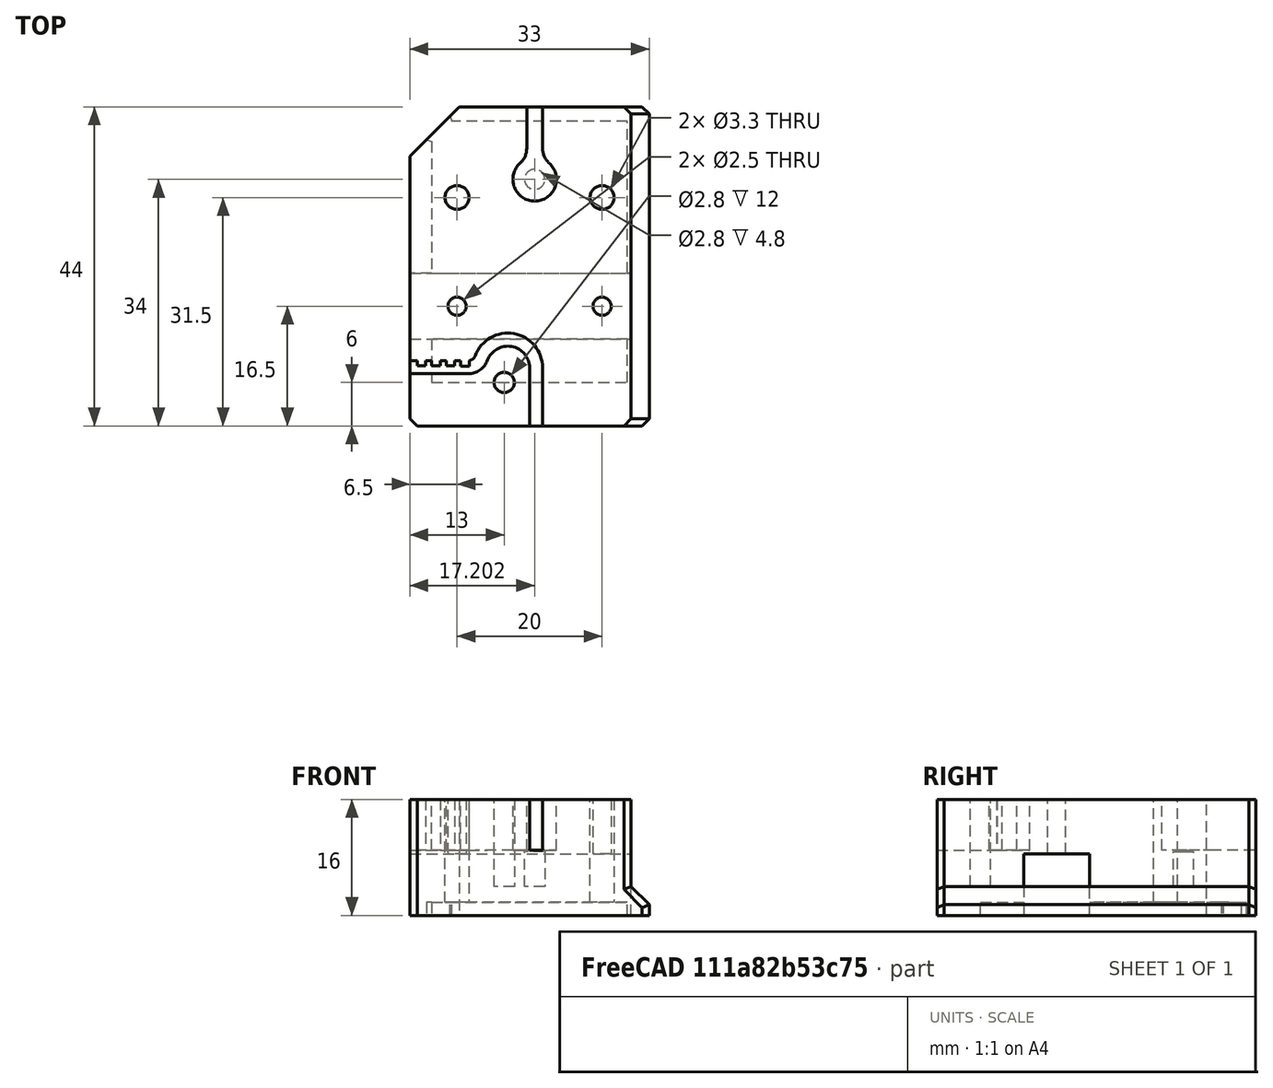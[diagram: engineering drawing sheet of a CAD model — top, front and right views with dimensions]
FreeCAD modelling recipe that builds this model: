
FCSTD DOCUMENT  (FreeCAD 0.19R)
Label: XjointBolted
License: All rights reserved
LicenseURL: http://en.wikipedia.org/wiki/All_rights_reserved
objects: Sketcher::SketchObject×10, PartDesign::Pocket×7, PartDesign::Pad×3, PartDesign::Chamfer×2, PartDesign::Body×1, Mesh::Feature×1
note: 35 computed .brp shape members not serialized (recipe doc carries the construction recipe); baked Part::Feature solids carry a one-line shape summary decoded from their .brp

FEATURE [Sketcher::SketchObject] Sketch005
  FullyConstrained = false
  MapMode = 5
  Support = -> [XY_Plane003]
  sketch-geometry (11):
    g0: LineSegment StartX=-37.8782 StartY=-3 StartZ=0 EndX=35.272 EndY=-3 EndZ=0
    g1: LineSegment StartX=35.272 StartY=-3 StartZ=0 EndX=35.272 EndY=-12 EndZ=0
    g2: LineSegment StartX=35.272 StartY=-12 StartZ=0 EndX=-37.8782 EndY=-12 EndZ=0
    g3: LineSegment StartX=-37.8782 StartY=-12 StartZ=0 EndX=-37.8782 EndY=-3 EndZ=0
    g4: LineSegment StartX=-44.3491 StartY=-7.5 StartZ=0 EndX=45.9652 EndY=-7.5 EndZ=0
    g5: Circle CenterX=-11.1499 CenterY=11.8637 CenterZ=0 NormalX=0 NormalY=0 NormalZ=1 AngleXU=0 Radius=1.40675
    g6: Circle CenterX=9.8811 CenterY=13.2001 CenterZ=0 NormalX=0 NormalY=0 NormalZ=1 AngleXU=0 Radius=2.36339
    g7: LineSegment StartX=-16.5 StartY=20 StartZ=0 EndX=16.5 EndY=20 EndZ=0
    g8: LineSegment StartX=16.5 StartY=20 StartZ=0 EndX=16.5 EndY=-24 EndZ=0
    g9: LineSegment StartX=16.5 StartY=-24 StartZ=0 EndX=-16.5 EndY=-24 EndZ=0
    g10: LineSegment StartX=-16.5 StartY=-24 StartZ=0 EndX=-16.5 EndY=20 EndZ=0
  constraints (22):
    c: Coincident(g0,g1)
    c: Coincident(g1,g2)
    c: Coincident(g2,g3)
    c: Coincident(g3,g0)
    c: Horizontal(g0)
    c: Horizontal(g2)
    c: Vertical(g1)
    c: Vertical(g3)
    c: Symmetric(g1,g0,g4)
    c: Distance(g1) = 9
    c: DistanceY(g4) = -7.5
    c: Coincident(g7,g8)
    c: Coincident(g8,g9)
    c: Coincident(g9,g10)
    c: Coincident(g10,g7)
    c: Horizontal(g7)
    c: Vertical(g8)
    c: Vertical(g10)
    c: Distance(g7) = 33
    c: DistanceY(g7) = 20
    c: DistanceY(g8) = -24
    c: Symmetric(g8,g9,g-2)
FEATURE [PartDesign::Pad] Pad002
  Direction = (1,1,1)
  Length = 16
  Length2 = 100
  Profile = -> Sketch005
  Type = 0
FEATURE [Sketcher::SketchObject] Sketch006  label="BottomPocket"
  FullyConstrained = true
  MapMode = 5
  Placement = pos=(0,0,0) rot=(1,0,0;3.14159rad)
  Support = -> [Pad002]
  sketch-geometry (4):
    g0: LineSegment StartX=-13.5 StartY=18 StartZ=0 EndX=13.5 EndY=18 EndZ=0
    g1: LineSegment StartX=13.5 StartY=18 StartZ=0 EndX=13.5 EndY=-18 EndZ=0
    g2: LineSegment StartX=13.5 StartY=-18 StartZ=0 EndX=-13.5 EndY=-18 EndZ=0
    g3: LineSegment StartX=-13.5 StartY=-18 StartZ=0 EndX=-13.5 EndY=18 EndZ=0
  constraints (11):
    c: Coincident(g0,g1)
    c: Coincident(g1,g2)
    c: Coincident(g2,g3)
    c: Coincident(g3,g0)
    c: Horizontal(g0)
    c: Horizontal(g2)
    c: Vertical(g1)
    c: Vertical(g3)
    c: Distance(g0) = 27
    c: Distance(g1) = 36
    c: Symmetric(g0,g2,g-1)
FEATURE [PartDesign::Pocket] Pocket002
  BaseFeature = -> Pad002
  Length = 1.8
  Length2 = 100
  Profile = -> Sketch006
  Type = 0
FEATURE [Sketcher::SketchObject] Sketch007  label="RailHole"
  FullyConstrained = false
  MapMode = 5
  Placement = pos=(-16.5,0,0) rot=(0.57735,-0.57735,-0.57735;2.0944rad)
  Support = -> [Pocket002]
  sketch-geometry (5):
    g0: LineSegment StartX=2.95 StartY=8.5 StartZ=0 EndX=12.05 EndY=8.5 EndZ=0
    g1: LineSegment StartX=12.05 StartY=8.5 StartZ=0 EndX=12.05 EndY=-2.55241 EndZ=0
    g2: LineSegment StartX=12.05 StartY=-2.55241 StartZ=0 EndX=2.95 EndY=-2.55241 EndZ=0
    g3: LineSegment StartX=2.95 StartY=-2.55241 StartZ=0 EndX=2.95 EndY=8.5 EndZ=0
    g4: LineSegment StartX=7.5 StartY=10.9531 StartZ=0 EndX=7.5 EndY=-7.76606 EndZ=0
  constraints (12):
    c: Coincident(g0,g1)
    c: Coincident(g1,g2)
    c: Coincident(g2,g3)
    c: Coincident(g3,g0)
    c: Horizontal(g0)
    c: Horizontal(g2)
    c: Vertical(g1)
    c: Vertical(g3)
    c: Distance(g0) = 9.1
    c: Symmetric(g0,g0,g4)
    c: DistanceX(g4) = 7.5
    c: DistanceY(g0) = 8.5
FEATURE [PartDesign::Pocket] Pocket003
  BaseFeature = -> Pocket002
  Length = 30.5
  Length2 = 100
  Profile = -> Sketch007
  Type = 0
FEATURE [Sketcher::SketchObject] Sketch009  label="BeltNotch"
  FullyConstrained = true
  MapMode = 5
  Placement = pos=(0,-24,0) rot=(1,0,0;1.5708rad)
  Support = -> [Pocket003]
  sketch-geometry (4):
    g0: LineSegment StartX=14 StartY=18.73 StartZ=0 EndX=14 EndY=4 EndZ=0
    g1: LineSegment StartX=14 StartY=4 StartZ=0 EndX=20.47 EndY=-2.47 EndZ=0
    g2: LineSegment StartX=20.47 StartY=-2.47 StartZ=0 EndX=20.47 EndY=18.73 EndZ=0
    g3: LineSegment StartX=20.47 StartY=18.73 StartZ=0 EndX=14 EndY=18.73 EndZ=0
  constraints (12):
    c: Vertical(g0)
    c: Coincident(g0,g1)
    c: Coincident(g1,g2)
    c: Vertical(g2)
    c: Coincident(g2,g3)
    c: Coincident(g3,g0)
    c: Horizontal(g3)
    c: DistanceX(g0) = 14
    c: DistanceY(g0) = 4
    c: Angle(g1) = -0.785398
    c: Distance(g3) = 6.47
    c: DistanceY(g2) = 18.73
FEATURE [Sketcher::SketchObject] Sketch012  label="BeltClamp"
  FullyConstrained = false
  MapMode = 5
  Placement = pos=(0,0,16) rot=(0,0,1;0rad)
  sketch-geometry (17):
    g0: LineSegment StartX=1.8 StartY=29.2485 StartZ=0 EndX=-0.4 EndY=29.2485 EndZ=0
    g1: LineSegment StartX=-0.4 StartY=29.2485 StartZ=0 EndX=-0.4 EndY=14.2485 EndZ=0
    g2: LineSegment StartX=1.8 StartY=29.2485 StartZ=0 EndX=1.8 EndY=14.2485 EndZ=0
    g3: ArcOfCircle CenterX=0.7 CenterY=10 CenterZ=0 NormalX=0 NormalY=0 NormalZ=1 AngleXU=0 Radius=3 StartAngle=2.30052 EndAngle=7.12425
    g4: ArcOfCircle CenterX=-3.1 CenterY=14.2485 CenterZ=0 NormalX=0 NormalY=0 NormalZ=1 AngleXU=0 Radius=2.7 StartAngle=5.44212 EndAngle=6.28319
    g5: ArcOfCircle CenterX=4.5 CenterY=14.2485 CenterZ=0 NormalX=0 NormalY=0 NormalZ=1 AngleXU=0 Radius=2.7 StartAngle=3.14159 EndAngle=3.98266
    g6: LineSegment StartX=0.7 StartY=39.9499 StartZ=0 EndX=0.7 EndY=-32.17 EndZ=0
    g7: LineSegment StartX=0 StartY=-26 StartZ=0 EndX=0 EndY=-16 EndZ=0
    g8: LineSegment StartX=1.8 StartY=-26 StartZ=0 EndX=1.8 EndY=-16 EndZ=0
    g9: LineSegment StartX=0 StartY=-26 StartZ=0 EndX=1.8 EndY=-26 EndZ=0
    g10: ArcOfCircle CenterX=-3 CenterY=-16 CenterZ=0 NormalX=0 NormalY=0 NormalZ=1 AngleXU=0 Radius=3 StartAngle=0 EndAngle=2.78378
    g11: ArcOfCircle CenterX=-3 CenterY=-16 CenterZ=0 NormalX=0 NormalY=0 NormalZ=1 AngleXU=0 Radius=4.8 StartAngle=0 EndAngle=2.78378
    g12: ArcOfCircle CenterX=-8.47782 CenterY=-13.9518 CenterZ=0 NormalX=0 NormalY=0 NormalZ=1 AngleXU=0 Radius=1.04822 StartAngle=4.71239 EndAngle=5.92537
    g13: ArcOfCircle CenterX=-8.47782 CenterY=-13.9518 CenterZ=0 NormalX=0 NormalY=0 NormalZ=1 AngleXU=0 Radius=2.84822 StartAngle=4.71239 EndAngle=5.92537
    g14: LineSegment StartX=-17.9078 StartY=-15 StartZ=0 EndX=-8.47782 EndY=-15 EndZ=0
    g15: LineSegment StartX=-17.9078 StartY=-16.8 StartZ=0 EndX=-8.47782 EndY=-16.8 EndZ=0
    g16: LineSegment StartX=-17.9078 StartY=-16.8 StartZ=0 EndX=-17.9078 EndY=-15 EndZ=0
  constraints (45):
    c: Coincident(g0,g1)
    c: Coincident(g0,g2)
    c: Distance(g0) = 2.2
    c: Tangent(g5,g2) = -1.5708
    c: Tangent(g4,g1) = 1.5708
    c: Tangent(g4,g3) = 1.5708
    c: Tangent(g5,g3) = 1.5708
    c: Diameter(g3) = 6
    c: Vertical(g6)
    c: PointOnObject(g3,g6)
    c: DistanceX(g6) = 0.7
    c: DistanceY(g6) = -32.17
    c: Vertical(g1)
    c: Vertical(g2)
    c: Equal(g2,g1)
    c: Symmetric(g0,g0,g6)
    c: DistanceY(g3) = 10
    c: Distance(g2) = 15
    c: Distance(g3,g3) = 4
    c: Vertical(g7)
    c: Vertical(g8)
    c: Coincident(g9,g7)
    c: Coincident(g9,g8)
    c: Horizontal(g9)
    c: Coincident(g11,g10)
    c: Coincident(g13,g12)
    c: Tangent(g12,g11) = 1.5708
    c: Tangent(g13,g10) = 1.5708
    c: Horizontal(g14)
    c: Tangent(g15,g13) = -1.5708
    c: Tangent(g14,g12) = -1.5708
    c: Horizontal(g15)
    c: Distance(g9) = 1.8
    c: Diameter(g10) = 6
    c: Tangent(g11,g8) = -1.5708
    c: Tangent(g10,g7) = -1.5708
    c: DistanceX(g10) = -3
    c: DistanceY(g7) = -16
    c: DistanceX(g12) = -8.47782
    c: DistanceY(g12) = -15
    c: Coincident(g16,g15)
    c: Coincident(g16,g14)
    c: Vertical(g16)
    c: Distance(g15) = 9.43
    c: Distance(g8) = 10
FEATURE [PartDesign::Pocket] Pocket004
  BaseFeature = -> Pocket003
  Length = 5
  Length2 = 100
  Profile = -> Sketch009
  Type = 1
FEATURE [Sketcher::SketchObject] Sketch011  label="holesBolts"
  FullyConstrained = true
  MapMode = 5
  Placement = pos=(0,0,16) rot=(0,0,1;0rad)
  Support = -> [Pocket004]
  sketch-geometry (4):
    g0: Circle CenterX=-10 CenterY=-7.5 CenterZ=0 NormalX=0 NormalY=0 NormalZ=1 AngleXU=0 Radius=1.25
    g1: Circle CenterX=10 CenterY=-7.5 CenterZ=0 NormalX=0 NormalY=0 NormalZ=1 AngleXU=0 Radius=1.25
    g2: Circle CenterX=-10 CenterY=7.5 CenterZ=0 NormalX=0 NormalY=0 NormalZ=1 AngleXU=0 Radius=1.65
    g3: Circle CenterX=10 CenterY=7.5 CenterZ=0 NormalX=0 NormalY=0 NormalZ=1 AngleXU=0 Radius=1.65
  constraints (9):
    c: Symmetric(g3,g2,g-2)
    c: Symmetric(g0,g1,g-2)
    c: Distance(g1,g0) = 20
    c: Distance(g3,g1) = 15
    c: Symmetric(g1,g3,g-1)
    c: Diameter(g2) = 3.3
    c: Equal(g2,g3)
    c: Diameter(g0) = 2.5
    c: Equal(g0,g1)
FEATURE [PartDesign::Pocket] Pocket005
  BaseFeature = -> Pocket004
  Length = 5
  Length2 = 100
  Profile = -> Sketch011
  Type = 1
FEATURE [PartDesign::Pocket] Pocket006
  BaseFeature = -> Pocket005
  Length = 7
  Length2 = 100
  Profile = -> Sketch012
  Type = 0
FEATURE [Sketcher::SketchObject] Sketch014  label="corner"
  FullyConstrained = false
  MapMode = 5
  Placement = pos=(0,0,16) rot=(0,0,1;0rad)
  sketch-geometry (3):
    g0: LineSegment StartX=-17.9525 StartY=11.746 StartZ=0 EndX=-6.3539 EndY=23.3446 EndZ=0
    g1: LineSegment StartX=-6.3539 StartY=23.3446 StartZ=0 EndX=-21.3456 EndY=27.3506 EndZ=0
    g2: LineSegment StartX=-21.3456 StartY=27.3506 StartZ=0 EndX=-17.9525 EndY=11.746 EndZ=0
  constraints (5):
    c: Coincident(g0,g1)
    c: Coincident(g1,g2)
    c: Coincident(g2,g0)
    c: Angle(g0) = 0.785398
    c: Distance(g-1,g0) = 21
FEATURE [Sketcher::SketchObject] Sketch015  label="clamphole1"
  FullyConstrained = false
  MapMode = 5
  Placement = pos=(0,0,9) rot=(0,0,1;0rad)
  sketch-geometry (2):
    g0: Circle CenterX=-3.5 CenterY=-18 CenterZ=0 NormalX=0 NormalY=0 NormalZ=1 AngleXU=0 Radius=1.4
    g1: Circle CenterX=0.701875 CenterY=10 CenterZ=0 NormalX=0 NormalY=0 NormalZ=1 AngleXU=0 Radius=1.4
  constraints (5):
    c: Diameter(g0) = 2.8
    c: Equal(g0,g1)
    c: DistanceY(g1) = 10
    c: DistanceX(g0) = -3.5
    c: DistanceY(g0) = -18
FEATURE [PartDesign::Pocket] Pocket007
  BaseFeature = -> Pocket006
  Length = 5
  Length2 = 100
  Profile = -> Sketch015
  Type = 4
FEATURE [Sketcher::SketchObject] Sketch016  label="teeth"
  FullyConstrained = false
  MapMode = 5
  Placement = pos=(0,0,16) rot=(0,0,1;0rad)
  Support = -> [Pocket007]
  sketch-geometry (29):
    g0: Circle CenterX=-20.9082 CenterY=-14.9653 CenterZ=0 NormalX=0 NormalY=0 NormalZ=1 AngleXU=0 Radius=0.5
    g1: Circle CenterX=-18.9082 CenterY=-14.9653 CenterZ=0 NormalX=0 NormalY=0 NormalZ=1 AngleXU=0 Radius=0.5
    g2: Circle CenterX=-16.9082 CenterY=-14.9653 CenterZ=0 NormalX=0 NormalY=0 NormalZ=1 AngleXU=0 Radius=0.5
    g3: Circle CenterX=-14.9082 CenterY=-14.9653 CenterZ=0 NormalX=0 NormalY=0 NormalZ=1 AngleXU=0 Radius=0.5
    g4: Circle CenterX=-12.9082 CenterY=-14.9653 CenterZ=0 NormalX=0 NormalY=0 NormalZ=1 AngleXU=0 Radius=0.5
    g5: Circle CenterX=-10.9082 CenterY=-14.9576 CenterZ=0 NormalX=0 NormalY=0 NormalZ=1 AngleXU=0 Radius=0.5
    g6: Circle CenterX=-8.90867 CenterY=-15.0023 CenterZ=0 NormalX=0 NormalY=0 NormalZ=1 AngleXU=0 Radius=0.5
    g7: LineSegment StartX=-20.9082 StartY=-14.9653 StartZ=0 EndX=-18.9082 EndY=-14.9653 EndZ=0
    g8: LineSegment StartX=-18.9082 StartY=-14.9653 StartZ=0 EndX=-16.9082 EndY=-14.9653 EndZ=0
    g9: LineSegment StartX=-16.9082 StartY=-14.9653 StartZ=0 EndX=-14.9082 EndY=-14.9653 EndZ=0
    g10: LineSegment StartX=-14.9082 StartY=-14.9653 StartZ=0 EndX=-12.9082 EndY=-14.9653 EndZ=0
    g11: LineSegment StartX=-12.9082 StartY=-14.9653 StartZ=0 EndX=-10.9082 EndY=-14.9576 EndZ=0
    g12: LineSegment StartX=-10.9082 StartY=-14.9576 StartZ=0 EndX=-8.90867 EndY=-15.0023 EndZ=0
    g13: LineSegment StartX=-15.5082 StartY=-14.2153 StartZ=0 EndX=-14.3082 EndY=-14.2153 EndZ=0
    g14: LineSegment StartX=-14.3082 StartY=-14.2153 StartZ=0 EndX=-14.3082 EndY=-15.7153 EndZ=0
    g15: LineSegment StartX=-14.3082 StartY=-15.7153 StartZ=0 EndX=-15.5082 EndY=-15.7153 EndZ=0
    g16: LineSegment StartX=-15.5082 StartY=-15.7153 StartZ=0 EndX=-15.5082 EndY=-14.2153 EndZ=0
    g17: LineSegment StartX=-13.5082 StartY=-14.2153 StartZ=0 EndX=-12.3082 EndY=-14.2153 EndZ=0
    g18: LineSegment StartX=-12.3082 StartY=-14.2153 StartZ=0 EndX=-12.3082 EndY=-15.7153 EndZ=0
    g19: LineSegment StartX=-12.3082 StartY=-15.7153 StartZ=0 EndX=-13.5082 EndY=-15.7153 EndZ=0
    g20: LineSegment StartX=-13.5082 StartY=-15.7153 StartZ=0 EndX=-13.5082 EndY=-14.2153 EndZ=0
    g21: LineSegment StartX=-11.5082 StartY=-14.2076 StartZ=0 EndX=-10.3082 EndY=-14.2076 EndZ=0
    g22: LineSegment StartX=-10.3082 StartY=-14.2076 StartZ=0 EndX=-10.3082 EndY=-15.7076 EndZ=0
    g23: LineSegment StartX=-10.3082 StartY=-15.7076 StartZ=0 EndX=-11.5082 EndY=-15.7076 EndZ=0
    g24: LineSegment StartX=-11.5082 StartY=-15.7076 StartZ=0 EndX=-11.5082 EndY=-14.2076 EndZ=0
    g25: LineSegment StartX=-9.50867 StartY=-14.2523 StartZ=0 EndX=-8.30867 EndY=-14.2523 EndZ=0
    g26: LineSegment StartX=-8.30867 StartY=-14.2523 StartZ=0 EndX=-8.30867 EndY=-15.7523 EndZ=0
    g27: LineSegment StartX=-8.30867 StartY=-15.7523 StartZ=0 EndX=-9.50867 EndY=-15.7523 EndZ=0
    g28: LineSegment StartX=-9.50867 StartY=-15.7523 StartZ=0 EndX=-9.50867 EndY=-14.2523 EndZ=0
  constraints (66):
    c: Coincident(g7,g0)
    c: Coincident(g7,g1)
    c: Horizontal(g7)
    c: Coincident(g7,g8)
    c: Coincident(g8,g2)
    c: Horizontal(g8)
    c: Coincident(g8,g9)
    c: Coincident(g9,g3)
    c: Horizontal(g9)
    c: Coincident(g9,g10)
    c: Coincident(g10,g4)
    c: Horizontal(g10)
    c: Coincident(g10,g11)
    c: Coincident(g11,g5)
    c: Coincident(g11,g12)
    c: Coincident(g12,g6)
    c: Equal(g7,g8)
    c: Equal(g8,g9)
    c: Equal(g9,g10)
    c: Equal(g10,g11)
    c: Equal(g11,g12)
    c: Distance(g12) = 2
    c: Coincident(g13,g14)
    c: Coincident(g14,g15)
    c: Coincident(g15,g16)
    c: Coincident(g16,g13)
    c: Horizontal(g13)
    c: Horizontal(g15)
    c: Vertical(g14)
    c: Vertical(g16)
    c: Coincident(g17,g18)
    c: Coincident(g18,g19)
    c: Coincident(g19,g20)
    c: Coincident(g20,g17)
    c: Horizontal(g17)
    c: Horizontal(g19)
    c: Vertical(g18)
    c: Vertical(g20)
    c: Coincident(g21,g22)
    c: Coincident(g22,g23)
    c: Coincident(g23,g24)
    c: Coincident(g24,g21)
    c: Horizontal(g21)
    c: Horizontal(g23)
    c: Vertical(g22)
    c: Vertical(g24)
    c: Coincident(g25,g26)
    c: Coincident(g26,g27)
    c: Coincident(g27,g28)
    c: Coincident(g28,g25)
    c: Horizontal(g25)
    c: Horizontal(g27)
    c: Vertical(g26)
    c: Vertical(g28)
    c: Equal(g13,g17)
    c: Equal(g17,g21)
    c: Equal(g21,g25)
    c: Equal(g28,g24)
    c: Equal(g24,g20)
    c: Equal(g20,g16)
    c: Symmetric(g15,g13,g3)
    c: Symmetric(g19,g17,g4)
    c: Symmetric(g23,g21,g5)
    c: Symmetric(g27,g25,g6)
    c: Distance(g17) = 1.2
    c: Distance(g18) = 1.5
FEATURE [PartDesign::Pocket] Pocket008
  BaseFeature = -> Pocket007
  Length = 5
  Length2 = 100
  Profile = -> Sketch014
  Type = 1
FEATURE [PartDesign::Pad] Pad003
  BaseFeature = -> Pocket008
  Direction = (1,1,1)
  Length = 7
  Length2 = 100
  Profile = -> Sketch016
  Reversed = true
  Type = 0
FEATURE [Sketcher::SketchObject] Sketch
  FullyConstrained = false
  MapMode = 5
  Placement = pos=(0,0,9) rot=(0,0,1;0rad)
  sketch-geometry (4):
    g0: LineSegment StartX=-4.04747 StartY=19.8268 StartZ=0 EndX=4.53362 EndY=19.8268 EndZ=0
    g1: LineSegment StartX=4.53362 StartY=19.8268 StartZ=0 EndX=4.53362 EndY=6.76661 EndZ=0
    g2: LineSegment StartX=4.53362 StartY=6.76661 StartZ=0 EndX=-4.04747 EndY=6.76661 EndZ=0
    g3: LineSegment StartX=-4.04747 StartY=6.76661 StartZ=0 EndX=-4.04747 EndY=19.8268 EndZ=0
  constraints (8):
    c: Coincident(g0,g1)
    c: Coincident(g1,g2)
    c: Coincident(g2,g3)
    c: Coincident(g3,g0)
    c: Horizontal(g0)
    c: Horizontal(g2)
    c: Vertical(g1)
    c: Vertical(g3)
FEATURE [PartDesign::Pad] Pad
  BaseFeature = -> Pad003
  Direction = (1,1,1)
  Length = 0.2
  Length2 = 100
  Profile = -> Sketch
  Reversed = true
  Type = 0
FEATURE [PartDesign::Chamfer] Chamfer
  Angle = 45
  Base = -> Pad [Edge105,Edge24,Edge26,Edge30,Edge2,Edge3,Edge4]
  BaseFeature = -> Pad
  ChamferType = 0
  FlipDirection = false
  Size = 1
  Size2 = 1
  SupportTransform = false
FEATURE [PartDesign::Chamfer] Chamfer001
  Angle = 45
  Base = -> Chamfer [Edge32,Edge30]
  BaseFeature = -> Chamfer
  ChamferType = 0
  FlipDirection = false
  Size = 1
  Size2 = 1
  SupportTransform = false
FEATURE [PartDesign::Body] Body003  label="Crail"
  Group = -> [Sketch005,Pad002,Sketch006,Pocket002,Sketch007,Pocket003,Sketch009,Sketch011,Sketch012,Pocket004,Pocket005,Pocket006,Sketch014,Sketch015,Pocket007,Sketch016,Pocket008,Pad003,Sketch,Pad,Chamfer,Chamfer001]
  Origin = -> Origin003
  Tip = -> Chamfer001
FEATURE [Mesh::Feature] Mesh  label="Chamfer001 (Meshed)"
